# Revit family: Haworth_ActiveComponents_SideCar_Basic_BUILD
name_source: partatom
category: Furniture Systems
revit_build: Autodesk Revit Architecture 2015 (Build: 20141119_1515(x64)
units: mm (PartAtom-declared; Revit-internal decimal feet)

## types (4) — shared parameters
Actual Depth = 18"
Actual Height = 8"
Actual Mounting Height = 33 1/2"
Actual Width = 72"
Assembly Code = E2020200
Custom Size = No
Description = Haworth - Active Components - Basic Side Car - 72w 8h
Divider 2 Cubbies Control = No
Divider 3 Cubbies Control = Yes
Height = 8"
Manufacturer = Haworth
Max. Height = 14"
Max. Width = 72"
Min. Height = 8"
Min. Width = 48"
Model = APSB, AQSB, ALSB, AZSB, ASSB, AYSB
Revision Number = 1
Shelf Height = 1/2"
Size = Verify Final Dim. w/ Haworth
Stanchion Offset = 4 1/4"
Support Offset = 30 13/16"
Sustainability Info = https://www.haworth.com
URL = http://www.haworth.com
URL - Product = http://www.haworth.com
Warranty = http://www.haworth.com
Width = 72"

## per-type parameters (varying)
| type | Freestanding Support Leg_Double | Left Leg Control | No Supports | Stanchion with Leg | Support Column |
| 72w 8h - Panel Mounted | No | No | Yes | No | No |
| 72w 8h - Panel Mounted with Column | No | No | No | No | Yes |
| 72w 8h - Freestanding | Yes | Yes | No | No | No |
| 72w 8h - Stanchion with Leg | No | Yes | No | Yes | No |

## geometry (parser evidence)
native form markers: Sweep x12
no freeform markers — native parametric forms only
